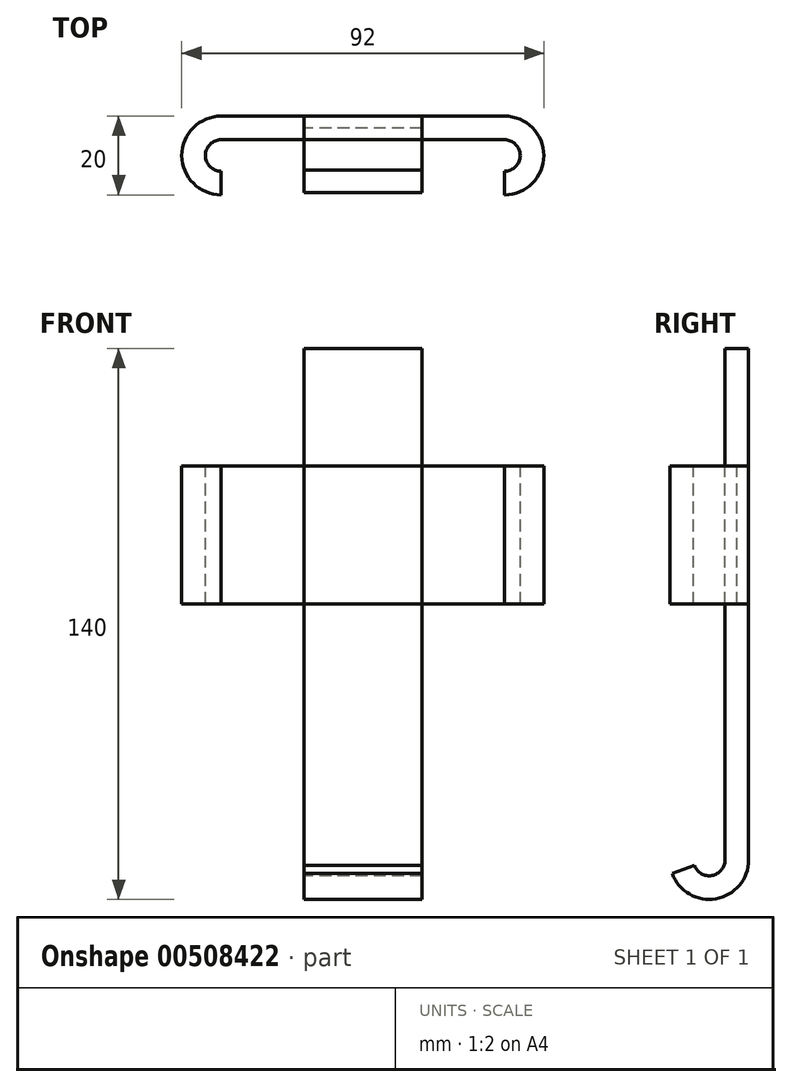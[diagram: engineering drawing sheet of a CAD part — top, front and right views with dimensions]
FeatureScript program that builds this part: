
annotation { "Feature Type Name" : "Feature", "Feature Type Description" : "" }
export const myFeature = defineFeature(function(context is Context, id is Id, definition is map)
    precondition{}
    {
        {
            var Q0;
            Q0=qCreatedBy(makeId("Front.planeOp"),FACE);
            var sketch = newSketch(context, id + "F0", { "sketchPlane" : qUnion([Q0])});
            skLineSegment(sketch, "E0.bottom", {"start": v(15, -50) * mm, "end": v(-15, -50) * mm});
            skLineSegment(sketch, "E0.top", {"start": v(15, 80) * mm, "end": v(-15, 80) * mm});
            skLineSegment(sketch, "E0.left", {"start": v(15, -50) * mm, "end": v(15, 80) * mm});
            skLineSegment(sketch, "E0.right", {"start": v(-15, -50) * mm, "end": v(-15, 80) * mm});
            skPoint(sketch, "E0.middle", {"position": v(0, 15) * mm});
            skLineSegment(sketch, "E1", {"start": v(0, 15) * mm, "end": v(0, 0) * mm, "construction": true});
            skSolve(sketch);
        }
        {
            var Q0;
            Q0=makeQuery(id+"F0.imprint","IMPRINT",FACE,{"disambiguationData":[TD([[makeQuery(id+"F0.imprint","IMPRINT",EDGE,{"derivedFrom":sQuery(id+"F0.wireOp",EDGE,"E0.bottom")}),-1.0]])]});
            extrude(context, id + "F1", {"entities" : qUnion([Q0]), "depth" : 6 * mm});
        }
        {
            var Q0;
            Q0=makeQuery(id+"F1.opExtrude","SWEPT_FACE",FACE,{"disambiguationData":[OSD([sQuery(id+"F0.wireOp",EDGE,"E0.right")])]});
            var sketch = newSketch(context, id + "F2", { "sketchPlane" : qUnion([Q0])});
            skArc(sketch, "E2", {"start": v(0, -50) * mm, "mid": v(8.26, -59.85) * mm, "end": v(19.4, -53.42) * mm});
            skArc(sketch, "E3", {"start": v(6, -50) * mm, "mid": v(9.3, -53.94) * mm, "end": v(13.76, -51.37) * mm});
            skLineSegment(sketch, "E4", {"start": v(13.76, -51.37) * mm, "end": v(19.4, -53.42) * mm});
            skLineSegment(sketch, "E5", {"start": v(10, -50) * mm, "end": v(13.76, -51.37) * mm, "construction": true});
            skLineSegment(sketch, "E6", {"start": v(6, -50) * mm, "end": v(0, -50) * mm});
            skSolve(sketch);
        }
        {
            var Q0;
            Q0=qSketchRegion(id+"F2",true);
            var Q1;
            Q1=makeQuery(id+"F1.opExtrude","SWEPT_FACE",FACE,{"disambiguationData":[OSD([sQuery(id+"F0.wireOp",EDGE,"E0.left")])]});
            extrude(context, id + "F3", {"entities" : qUnion([Q0]), "operationType" : NewBodyOperationType.ADD, "endBound" : BoundingType.UP_TO_SURFACE, "oppositeDirection" : true, "endBoundEntityFace" : qUnion([Q1]), "depth" : 25 * mm});
        }
        {
            var Q0;
            Q0=qCreatedBy(makeId("Front.planeOp"),FACE);
            var sketch = newSketch(context, id + "F4", { "sketchPlane" : qUnion([Q0])});
            skLineSegment(sketch, "E7.bottom", {"start": v(36, 50.07) * mm, "end": v(-36, 50.07) * mm});
            skLineSegment(sketch, "E7.top", {"start": v(36, 15.07) * mm, "end": v(-36, 15.07) * mm});
            skLineSegment(sketch, "E7.left", {"start": v(36, 50.07) * mm, "end": v(36, 15.07) * mm});
            skLineSegment(sketch, "E7.right", {"start": v(-36, 50.07) * mm, "end": v(-36, 15.07) * mm});
            skPoint(sketch, "E7.middle", {"position": v(0, 32.57) * mm});
            skLineSegment(sketch, "E8", {"start": v(0, 32.57) * mm, "end": v(0, 0) * mm, "construction": true});
            skSolve(sketch);
        }
        {
            var Q0;
            Q0=qSketchRegion(id+"F4",true);
            var Q1;
            Q1=makeQuery(id+"F1.opExtrude","CAP_FACE",FACE,{"disambiguationData":[OSD([sQuery(id+"F0.wireOp",EDGE,"E0.bottom"),sQuery(id+"F0.wireOp",EDGE,"E0.top"),sQuery(id+"F0.wireOp",EDGE,"E0.left"),sQuery(id+"F0.wireOp",EDGE,"E0.right")])],"isStart":false});
            extrude(context, id + "F5", {"entities" : qUnion([Q0]), "endBound" : BoundingType.UP_TO_SURFACE, "endBoundEntityFace" : qUnion([Q1]), "depth" : 25 * mm});
        }
        {
            var Q0;
            Q0=makeQuery(id+"F5.opExtrude","SWEPT_FACE",FACE,{"disambiguationData":[OSD([sQuery(id+"F4.wireOp",EDGE,"E7.bottom")])]});
            var sketch = newSketch(context, id + "F6", { "sketchPlane" : qUnion([Q0])});
            skArc(sketch, "E9", {"start": v(-36, 0) * mm, "mid": v(-46, -10) * mm, "end": v(-36, -20) * mm});
            skArc(sketch, "E10", {"start": v(-36, -6) * mm, "mid": v(-40, -10) * mm, "end": v(-36, -14) * mm});
            skLineSegment(sketch, "E11", {"start": v(-36, -20) * mm, "end": v(-36, -14) * mm});
            skLineSegment(sketch, "E12", {"start": v(-36, -6) * mm, "end": v(-36, 0) * mm});
            skArc(sketch, "E13", {"start": v(36, 0) * mm, "mid": v(46, -10) * mm, "end": v(36, -20) * mm});
            skArc(sketch, "E14", {"start": v(36, -6) * mm, "mid": v(40, -10) * mm, "end": v(36, -14) * mm});
            skLineSegment(sketch, "E15", {"start": v(36, -20) * mm, "end": v(36, -14) * mm});
            skLineSegment(sketch, "E16", {"start": v(36, -6) * mm, "end": v(36, 0) * mm});
            skSolve(sketch);
        }
        {
            var Q0;
            Q0=qSketchRegion(id+"F6",true);
            var Q1;
            Q1=makeQuery(id+"F5.opExtrude","SWEPT_FACE",FACE,{"disambiguationData":[OSD([sQuery(id+"F4.wireOp",EDGE,"E7.top")])]});
            extrude(context, id + "F7", {"entities" : qUnion([Q0]), "operationType" : NewBodyOperationType.ADD, "endBound" : BoundingType.UP_TO_SURFACE, "oppositeDirection" : true, "endBoundEntityFace" : qUnion([Q1]), "depth" : 25 * mm});
        }
        {
            var Q0;
            Q0=makeQuery(id+"F1.opExtrude","CAP_FACE",FACE,{"disambiguationData":[OSD([sQuery(id+"F0.wireOp",EDGE,"E0.bottom"),sQuery(id+"F0.wireOp",EDGE,"E0.top"),sQuery(id+"F0.wireOp",EDGE,"E0.left"),sQuery(id+"F0.wireOp",EDGE,"E0.right")])],"isStart":false});
            var sketch = newSketch(context, id + "F8", { "sketchPlane" : qUnion([Q0])});
            skLineSegment(sketch, "E17.bottom", {"start": v(15, 15.07) * mm, "end": v(-15, 15.07) * mm});
            skLineSegment(sketch, "E17.top", {"start": v(15, 50.07) * mm, "end": v(-15, 50.07) * mm});
            skLineSegment(sketch, "E17.left", {"start": v(15, 15.07) * mm, "end": v(15, 50.07) * mm});
            skLineSegment(sketch, "E17.right", {"start": v(-15, 15.07) * mm, "end": v(-15, 50.07) * mm});
            skSolve(sketch);
        }
        {
            var Q0;
            Q0=makeQuery(id+"F8.imprint","IMPRINT",FACE,{"disambiguationData":[TD([[makeQuery(id+"F8.imprint","IMPRINT",EDGE,{"derivedFrom":sQuery(id+"F8.wireOp",EDGE,"E17.bottom")}),-1.0]])]});
            extrude(context, id + "F9", {"entities" : qUnion([Q0]), "operationType" : NewBodyOperationType.REMOVE, "oppositeDirection" : true, "depth" : 3 * mm});
        }
        {
            var Q0;
            Q0=makeQuery(id+"F1.opExtrude","SWEPT_BODY",BODY,{"disambiguationData":[OSD([sQuery(id+"F0.wireOp",EDGE,"E0.bottom"),sQuery(id+"F0.wireOp",EDGE,"E0.top"),sQuery(id+"F0.wireOp",EDGE,"E0.left"),sQuery(id+"F0.wireOp",EDGE,"E0.right")])]});
            var Q1;
            Q1=makeQuery(id+"F5.opExtrude","SWEPT_BODY",BODY,{"disambiguationData":[OSD([sQuery(id+"F4.wireOp",EDGE,"E7.bottom"),sQuery(id+"F4.wireOp",EDGE,"E7.top"),sQuery(id+"F4.wireOp",EDGE,"E7.left"),sQuery(id+"F4.wireOp",EDGE,"E7.right")])]});
            booleanBodies(context, id + "F10", {"operationType" : BooleanOperationType.SUBTRACTION, "tools" : qUnion([Q0]), "targets" : qUnion([Q1]), "keepTools" : true});
        }
    });
